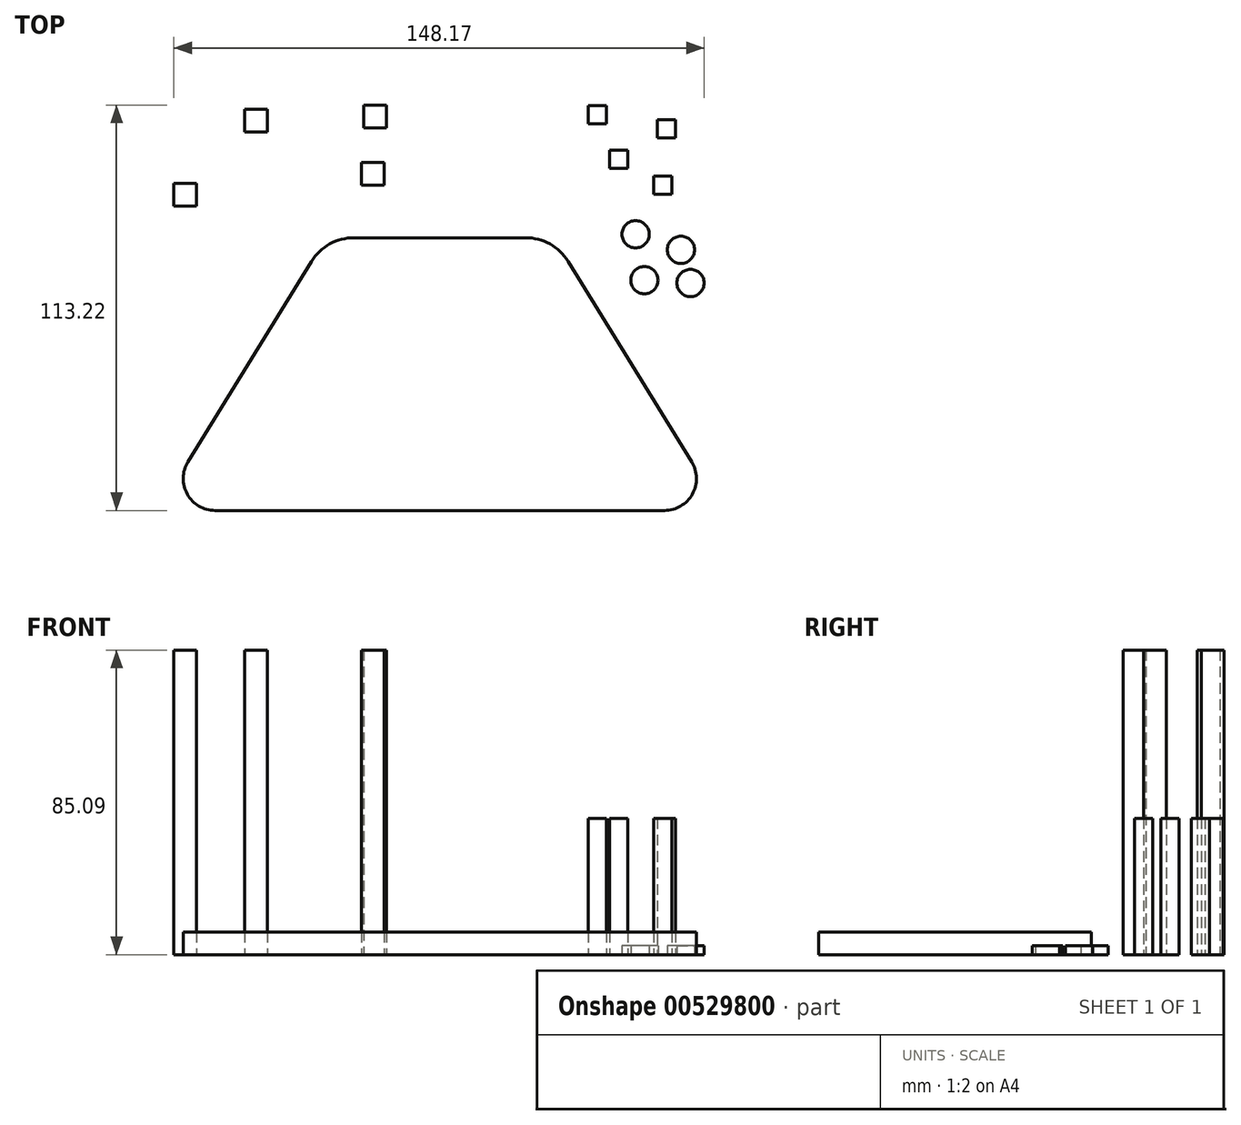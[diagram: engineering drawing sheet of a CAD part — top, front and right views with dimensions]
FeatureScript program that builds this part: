
annotation { "Feature Type Name" : "Feature", "Feature Type Description" : "" }
export const myFeature = defineFeature(function(context is Context, id is Id, definition is map)
    precondition{}
    {
        {
            var Q0;
            Q0=qCreatedBy(makeId("Top.planeOp"),FACE);
            var sketch = newSketch(context, id + "F0", { "sketchPlane" : qUnion([Q0])});
            skLineSegment(sketch, "E0.bottom", {"start": v(-23.95, 38.1) * mm, "end": v(23.95, 38.1) * mm});
            skLineSegment(sketch, "E0.top", {"start": v(-31.75, -38.1) * mm, "end": v(31.75, -38.1) * mm});
            skLineSegment(sketch, "E0.left", {"start": v(-31.75, 38.1) * mm, "end": v(-31.75, -38.1) * mm});
            skLineSegment(sketch, "E0.right", {"start": v(31.75, 38.1) * mm, "end": v(31.75, -38.1) * mm});
            skPoint(sketch, "E0.middle", {"position": v(0, 0) * mm});
            skLineSegment(sketch, "E1", {"start": v(-31.75, -38.1) * mm, "end": v(-62.81, -38.1) * mm});
            skLineSegment(sketch, "E2", {"start": v(31.75, -38.1) * mm, "end": v(62.81, -38.1) * mm});
            skLineSegment(sketch, "E3", {"start": v(-70.38, -24.54) * mm, "end": v(-35.84, 31.46) * mm});
            skLineSegment(sketch, "E4", {"start": v(35.84, 31.46) * mm, "end": v(70.38, -24.54) * mm});
            skPoint(sketch, "E5.visualSharp", {"position": v(-31.75, 38.1) * mm});
            skArc(sketch, "E5.filletArc", {"start": v(-23.95, 38.1) * mm, "mid": v(-30.76, 36.33) * mm, "end": v(-35.84, 31.46) * mm});
            skPoint(sketch, "E6.visualSharp", {"position": v(31.75, 38.1) * mm});
            skArc(sketch, "E6.filletArc", {"start": v(35.84, 31.46) * mm, "mid": v(30.76, 36.33) * mm, "end": v(23.95, 38.1) * mm});
            skPoint(sketch, "E7.visualSharp", {"position": v(-78.74, -38.1) * mm});
            skArc(sketch, "E7.filletArc", {"start": v(-70.38, -24.54) * mm, "mid": v(-70.58, -33.54) * mm, "end": v(-62.81, -38.1) * mm});
            skPoint(sketch, "E8.visualSharp", {"position": v(78.74, -38.1) * mm});
            skArc(sketch, "E8.filletArc", {"start": v(62.81, -38.1) * mm, "mid": v(70.58, -33.54) * mm, "end": v(70.38, -24.54) * mm});
            skSolve(sketch);
        }
        {
            var Q0;
            {var subQ7=sQuery(id+"F0.wireOp",EDGE,"E0.bottom");Q0=makeQuery(id+"F0.imprint","IMPRINT",FACE,{"disambiguationData":[TD([[makeQuery(id+"F0.imprint","IMPRINT",EDGE,{"derivedFrom":subQ7}),-1.0]])]});}
            var Q1;
            {var subQ4=sQuery(id+"F0.wireOp",EDGE,"E1");Q1=makeQuery(id+"F0.imprint","IMPRINT",FACE,{"disambiguationData":[TD([[makeQuery(id+"F0.imprint","IMPRINT",EDGE,{"derivedFrom":subQ4}),-1.0]])]});}
            var Q2;
            {var subQ4=sQuery(id+"F0.wireOp",EDGE,"E2");Q2=makeQuery(id+"F0.imprint","IMPRINT",FACE,{"disambiguationData":[TD([[makeQuery(id+"F0.imprint","IMPRINT",EDGE,{"derivedFrom":subQ4}),1.0]])]});}
            extrude(context, id + "F1", {"entities" : qUnion([Q0, Q1, Q2]), "depth" : 6.35 * mm, "offsetDistance" : 25.4 * mm});
        }
        {
            var Q0;
            Q0=qCreatedBy(makeId("Top.planeOp"),FACE);
            var sketch = newSketch(context, id + "F2", { "sketchPlane" : qUnion([Q0])});
            skLineSegment(sketch, "E9.bottom", {"start": v(-48.18, 67.7) * mm, "end": v(-54.53, 67.7) * mm});
            skLineSegment(sketch, "E9.top", {"start": v(-48.18, 74.04) * mm, "end": v(-54.53, 74.04) * mm});
            skLineSegment(sketch, "E9.left", {"start": v(-48.18, 67.7) * mm, "end": v(-48.18, 74.04) * mm});
            skLineSegment(sketch, "E9.right", {"start": v(-54.53, 67.7) * mm, "end": v(-54.53, 74.04) * mm});
            skPoint(sketch, "E9.middle", {"position": v(-51.35, 70.87) * mm});
            skLineSegment(sketch, "E10.bottom", {"start": v(-14.96, 68.77) * mm, "end": v(-21.31, 68.77) * mm});
            skLineSegment(sketch, "E10.top", {"start": v(-14.96, 75.12) * mm, "end": v(-21.31, 75.12) * mm});
            skLineSegment(sketch, "E10.left", {"start": v(-14.96, 68.77) * mm, "end": v(-14.96, 75.12) * mm});
            skLineSegment(sketch, "E10.right", {"start": v(-21.31, 68.77) * mm, "end": v(-21.31, 75.12) * mm});
            skPoint(sketch, "E10.middle", {"position": v(-18.14, 71.95) * mm});
            skLineSegment(sketch, "E11.bottom", {"start": v(-15.57, 52.72) * mm, "end": v(-21.92, 52.72) * mm});
            skLineSegment(sketch, "E11.top", {"start": v(-15.57, 59.07) * mm, "end": v(-21.92, 59.07) * mm});
            skLineSegment(sketch, "E11.left", {"start": v(-15.57, 52.72) * mm, "end": v(-15.57, 59.07) * mm});
            skLineSegment(sketch, "E11.right", {"start": v(-21.92, 52.72) * mm, "end": v(-21.92, 59.07) * mm});
            skPoint(sketch, "E11.middle", {"position": v(-18.74, 55.9) * mm});
            skLineSegment(sketch, "E12.bottom", {"start": v(-67.95, 46.97) * mm, "end": v(-74.3, 46.97) * mm});
            skLineSegment(sketch, "E12.top", {"start": v(-67.95, 53.32) * mm, "end": v(-74.3, 53.32) * mm});
            skLineSegment(sketch, "E12.left", {"start": v(-67.95, 46.97) * mm, "end": v(-67.95, 53.32) * mm});
            skLineSegment(sketch, "E12.right", {"start": v(-74.3, 46.97) * mm, "end": v(-74.3, 53.32) * mm});
            skPoint(sketch, "E12.middle", {"position": v(-71.13, 50.14) * mm});
            skSolve(sketch);
        }
        {
            var Q0;
            Q0 = qSketchRegion(id + "F2", true);
            extrude(context, id + "F3", {"entities" : qUnion([Q0]), "depth" : 85.1 * mm, "offsetDistance" : 25.4 * mm});
        }
        {
            var Q0;
            Q0=qCreatedBy(makeId("Top.planeOp"),FACE);
            var sketch = newSketch(context, id + "F4", { "sketchPlane" : qUnion([Q0])});
            skLineSegment(sketch, "E13.bottom", {"start": v(46.54, 69.87) * mm, "end": v(41.46, 69.87) * mm});
            skLineSegment(sketch, "E13.top", {"start": v(46.54, 74.95) * mm, "end": v(41.46, 74.95) * mm});
            skLineSegment(sketch, "E13.left", {"start": v(46.54, 69.87) * mm, "end": v(46.54, 74.95) * mm});
            skLineSegment(sketch, "E13.right", {"start": v(41.46, 69.87) * mm, "end": v(41.46, 74.95) * mm});
            skPoint(sketch, "E13.middle", {"position": v(44, 72.4) * mm});
            skLineSegment(sketch, "E14.bottom", {"start": v(65.85, 66) * mm, "end": v(60.77, 66) * mm});
            skLineSegment(sketch, "E14.top", {"start": v(65.85, 71.08) * mm, "end": v(60.77, 71.08) * mm});
            skLineSegment(sketch, "E14.left", {"start": v(65.85, 66) * mm, "end": v(65.85, 71.08) * mm});
            skLineSegment(sketch, "E14.right", {"start": v(60.77, 66) * mm, "end": v(60.77, 71.08) * mm});
            skPoint(sketch, "E14.middle", {"position": v(63.31, 68.54) * mm});
            skLineSegment(sketch, "E15.bottom", {"start": v(52.53, 57.5) * mm, "end": v(47.45, 57.5) * mm});
            skLineSegment(sketch, "E15.top", {"start": v(52.53, 62.59) * mm, "end": v(47.45, 62.59) * mm});
            skLineSegment(sketch, "E15.left", {"start": v(52.53, 57.5) * mm, "end": v(52.53, 62.59) * mm});
            skLineSegment(sketch, "E15.right", {"start": v(47.45, 57.5) * mm, "end": v(47.45, 62.59) * mm});
            skPoint(sketch, "E15.middle", {"position": v(49.99, 60.05) * mm});
            skLineSegment(sketch, "E16.bottom", {"start": v(64.85, 50.18) * mm, "end": v(59.77, 50.18) * mm});
            skLineSegment(sketch, "E16.top", {"start": v(64.85, 55.26) * mm, "end": v(59.77, 55.26) * mm});
            skLineSegment(sketch, "E16.left", {"start": v(64.85, 50.18) * mm, "end": v(64.85, 55.26) * mm});
            skLineSegment(sketch, "E16.right", {"start": v(59.77, 50.18) * mm, "end": v(59.77, 55.26) * mm});
            skPoint(sketch, "E16.middle", {"position": v(62.31, 52.72) * mm});
            skSolve(sketch);
        }
        {
            var Q0;
            Q0 = qSketchRegion(id + "F4", true);
            extrude(context, id + "F5", {"entities" : qUnion([Q0]), "depth" : 38.1 * mm, "offsetDistance" : 25.4 * mm});
        }
        {
            var Q0;
            Q0=qCreatedBy(makeId("Top.planeOp"),FACE);
            var sketch = newSketch(context, id + "F6", { "sketchPlane" : qUnion([Q0])});
            skCircle(sketch, "E17", {"center": v(54.71, 39.04) * mm, "radius": 3.8 * mm});
            skCircle(sketch, "E18", {"center": v(67.38, 34.72) * mm, "radius": 3.8 * mm});
            skCircle(sketch, "E19", {"center": v(57.17, 26.23) * mm, "radius": 3.8 * mm});
            skCircle(sketch, "E20", {"center": v(70.06, 25.44) * mm, "radius": 3.8 * mm});
            skSolve(sketch);
        }
        {
            var Q0;
            Q0 = qSketchRegion(id + "F6", true);
            extrude(context, id + "F7", {"entities" : qUnion([Q0]), "depth" : 2.54 * mm, "offsetDistance" : 25.4 * mm});
        }
    });
